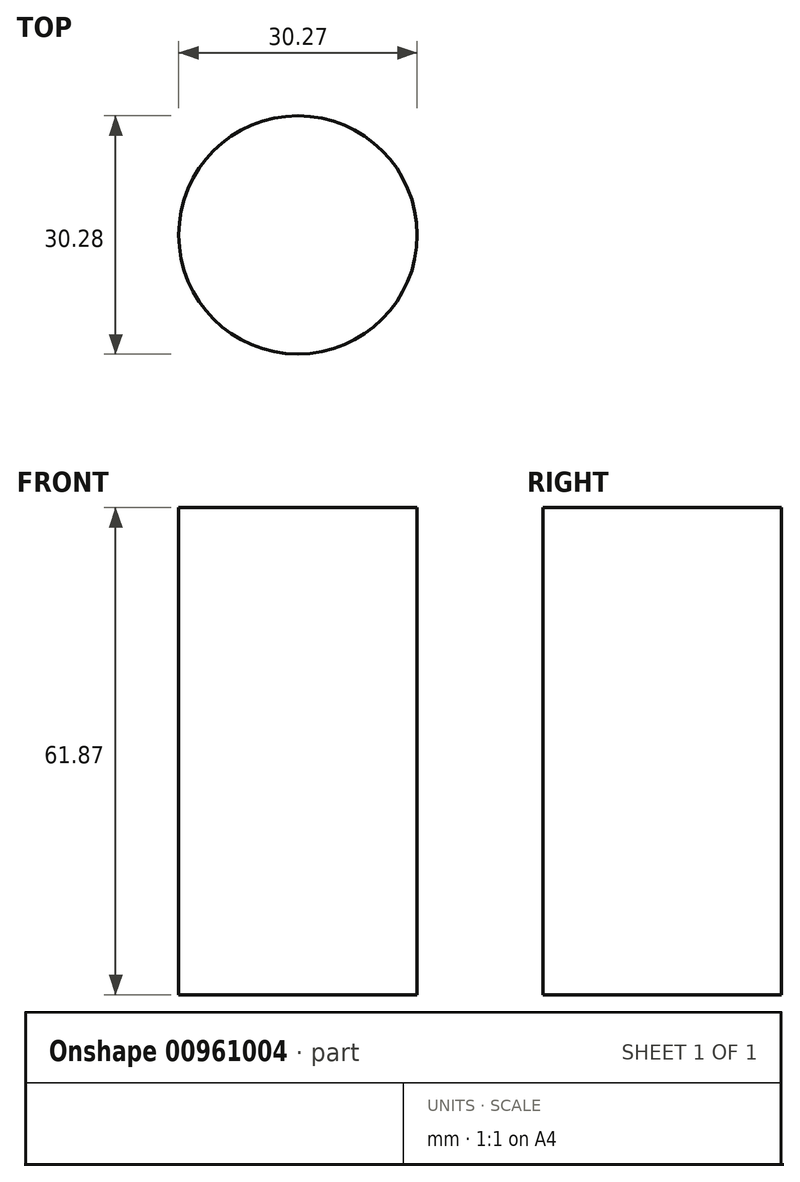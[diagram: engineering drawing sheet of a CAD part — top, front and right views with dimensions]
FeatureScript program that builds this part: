
annotation { "Feature Type Name" : "Feature", "Feature Type Description" : "" }
export const myFeature = defineFeature(function(context is Context, id is Id, definition is map)
    precondition{}
    {
        {
            var Q0;
            Q0=qCreatedBy(makeId("Front.planeOp"),FACE);
            var sketch = newSketch(context, id + "F0", { "sketchPlane" : qUnion([Q0])});
            skLineSegment(sketch, "E0", {"start": v(8.18, 61.87) * mm, "end": v(8.18, 29.77) * mm});
            skLineSegment(sketch, "E1", {"start": v(8.58, 29.98) * mm, "end": v(23.31, 29.98) * mm});
            skLineSegment(sketch, "E2", {"start": v(23.31, 29.98) * mm, "end": v(23.31, 61.87) * mm});
            skLineSegment(sketch, "E3", {"start": v(23.31, 61.87) * mm, "end": v(8.18, 61.87) * mm});
            skLineSegment(sketch, "E4", {"start": v(23.31, 29.98) * mm, "end": v(23.31, 0) * mm});
            skLineSegment(sketch, "E5", {"start": v(23.31, 0) * mm, "end": v(8.18, 0) * mm});
            skLineSegment(sketch, "E6", {"start": v(8.18, 0) * mm, "end": v(8.18, 29.77) * mm});
            skSolve(sketch);
        }
        {
            var Q0;
            Q0=makeQuery(id+"F0.imprint","IMPRINT",FACE,{"disambiguationData":[TD([[makeQuery(id+"F0.imprint","IMPRINT",EDGE,{"derivedFrom":sQuery(id+"F0.wireOp",EDGE,"E0")}),1.0]])]});
            var Q1;
            Q1=sQuery(id+"F0.wireOp",EDGE,"E2");
            revolve(context, id + "F1", {"surfaceOperationType" : NewSurfaceOperationType.NEW, "entities" : qUnion([Q0]), "axis" : qUnion([Q1]), "revolveType" : RevolveType.FULL});
        }
    });
